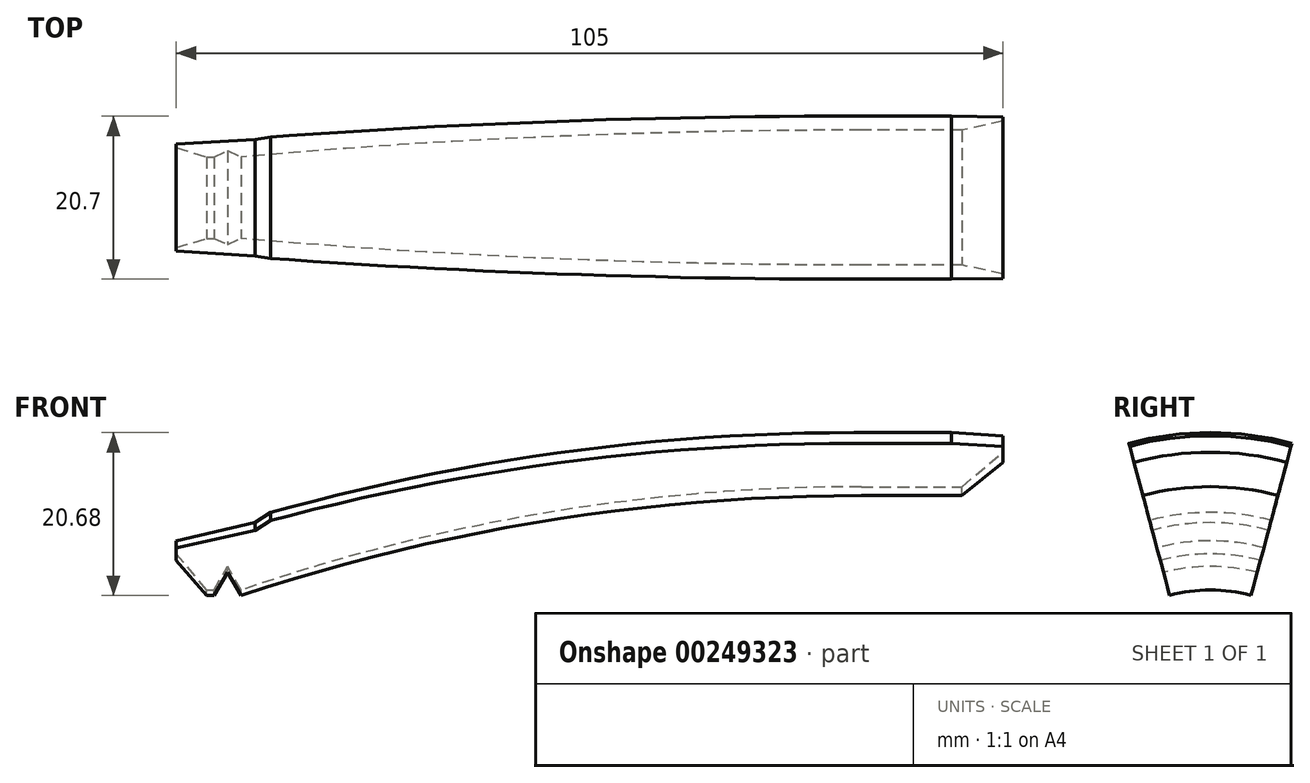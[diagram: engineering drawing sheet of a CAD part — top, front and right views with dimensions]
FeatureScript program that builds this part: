
annotation { "Feature Type Name" : "Feature", "Feature Type Description" : "" }
export const myFeature = defineFeature(function(context is Context, id is Id, definition is map)
    precondition{}
    {
        {
            var Q0;
            Q0=qCreatedBy(makeId("Front.planeOp"),FACE);
            var sketch = newSketch(context, id + "F0", { "sketchPlane" : qUnion([Q0])});
            skLineSegment(sketch, "E0", {"start": v(-5.22, 33.12) * mm, "end": v(-18, 33.12) * mm});
            skLineSegment(sketch, "E1", {"start": v(0, 37.5) * mm, "end": v(0, 39.6) * mm});
            skLineSegment(sketch, "E2", {"start": v(0, 39.6) * mm, "end": v(-6.54, 40) * mm});
            skLineSegment(sketch, "E3", {"start": v(-6.54, 40) * mm, "end": v(-18.91, 40) * mm});
            skLineSegment(sketch, "E4", {"start": v(0, 0) * mm, "end": v(-138.02, 0) * mm});
            skLineSegment(sketch, "E5", {"start": v(-105, 26.6) * mm, "end": v(-90.66, 30.48) * mm});
            skLineSegment(sketch, "E6", {"start": v(-105, 26.6) * mm, "end": v(-105, 24.6) * mm});
            skLineSegment(sketch, "E7", {"start": v(-105, 24.6) * mm, "end": v(-101.14, 20) * mm});
            skLineSegment(sketch, "E8", {"start": v(0, 37.5) * mm, "end": v(-5.22, 33.12) * mm});
            skPoint(sketch, "E9.orphan", {"position": v(0, 33.12) * mm});
            skLineSegment(sketch, "E10", {"start": v(-97.46, 29.14) * mm, "end": v(-105.18, 27.05) * mm, "construction": true});
            skLineSegment(sketch, "E11", {"start": v(-105.18, 27.05) * mm, "end": v(-105, 26.37) * mm, "construction": true});
            skLineSegment(sketch, "E12", {"start": v(-105, 26.37) * mm, "end": v(-97.28, 28.46) * mm, "construction": true});
            skLineSegment(sketch, "E13", {"start": v(-97.46, 29.14) * mm, "end": v(-97.28, 28.46) * mm, "construction": true});
            skLineSegment(sketch, "E14", {"start": v(-101.14, 20) * mm, "end": v(-100.23, 20) * mm});
            skLineSegment(sketch, "E15", {"start": v(-100.23, 20) * mm, "end": v(-98.5, 23) * mm});
            skLineSegment(sketch, "E16", {"start": v(-98.5, 23) * mm, "end": v(-96.77, 20) * mm});
            skPoint(sketch, "E17.visualSharp", {"position": v(-54.5, 33.12) * mm});
            skPoint(sketch, "E18.visualSharp", {"position": v(-55.42, 40) * mm});
            skArc(sketch, "E18.filletArc", {"start": v(-18.91, 40) * mm, "mid": v(-55.1, 37.6) * mm, "end": v(-90.66, 30.48) * mm});
            skArc(sketch, "E19", {"start": v(-18, 33.12) * mm, "mid": v(-57.93, 29.82) * mm, "end": v(-96.77, 20) * mm});
            skSolve(sketch);
        }
        {
            var Q0;
            Q0=makeQuery(id+"F0.imprint","IMPRINT",FACE,{"disambiguationData":[TD([[makeQuery(id+"F0.imprint","IMPRINT",EDGE,{"derivedFrom":sQuery(id+"F0.wireOp",EDGE,"E0")}),-1.0]])]});
            var Q1;
            Q1=sQuery(id+"F0.wireOp",EDGE,"E4");
            revolve(context, id + "F1", {"entities" : qUnion([Q0]), "axis" : qUnion([Q1]), "revolveType" : RevolveType.SYMMETRIC, "angle" : 30 * degree});
        }
        {
            var Q0;
            Q0=qCreatedBy(makeId("Front.planeOp"),FACE);
            var sketch = newSketch(context, id + "F2", { "sketchPlane" : qUnion([Q0])});
            skLineSegment(sketch, "E20", {"start": v(0, 0) * mm, "end": v(-119.57, 0) * mm, "construction": true});
            skLineSegment(sketch, "E21.0", {"start": v(-105, 26.25) * mm, "end": v(-105, 26.6) * mm});
            skLineSegment(sketch, "E22", {"start": v(-105, 26.6) * mm, "end": v(-93, 29.84) * mm});
            skPoint(sketch, "E23.orphan", {"position": v(-105, 25.7) * mm});
            skLineSegment(sketch, "E24", {"start": v(-105, 26.25) * mm, "end": v(-95, 28.56) * mm});
            skLineSegment(sketch, "E25", {"start": v(-95, 28.56) * mm, "end": v(-93, 29.84) * mm});
            skSolve(sketch);
        }
        {
            var Q0;
            Q0=makeQuery(id+"F2.imprint","IMPRINT",FACE,{"disambiguationData":[TD([[makeQuery(id+"F2.imprint","IMPRINT",EDGE,{"derivedFrom":sQuery(id+"F2.wireOp",EDGE,"E21.0")}),-1.0]])]});
            var Q1;
            Q1=sQuery(id+"F2.wireOp",EDGE,"E20");
            revolve(context, id + "F3", {"operationType" : NewBodyOperationType.REMOVE, "entities" : qUnion([Q0]), "axis" : qUnion([Q1]), "revolveType" : RevolveType.FULL, "oppositeDirection" : true});
        }
    });
